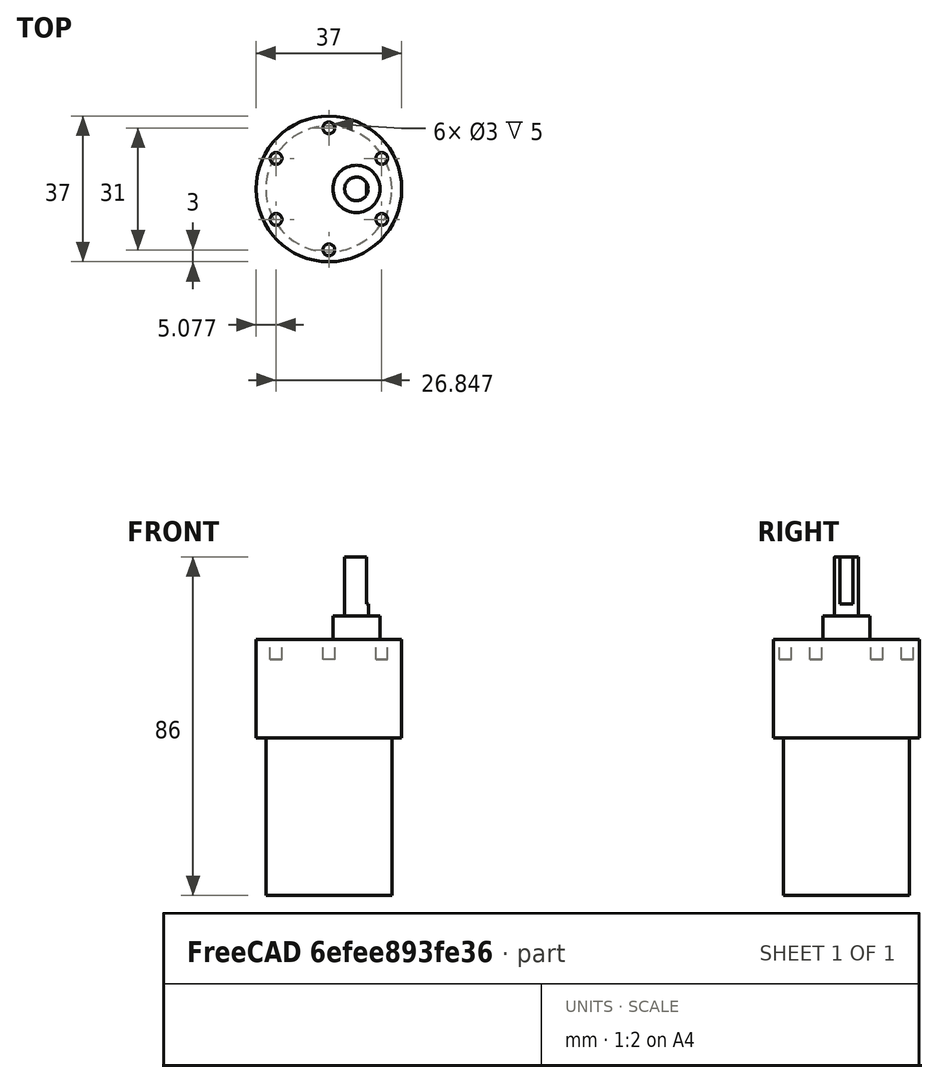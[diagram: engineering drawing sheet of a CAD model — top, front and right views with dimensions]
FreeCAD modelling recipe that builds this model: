
FCSTD DOCUMENT  (FreeCAD 0.17R13522 (Git))
Label: DC_Gear_Motor_37mm
License: All rights reserved
LicenseURL: http://en.wikipedia.org/wiki/All_rights_reserved
objects: Part::Cylinder×5, Part::MultiFuse×2, Part::Box×1, Part::FeaturePython×1, Part::Cut×1
note: 10 computed .brp shape members not serialized (recipe doc carries the construction recipe); baked Part::Feature solids carry a one-line shape summary decoded from their .brp

FEATURE [Part::Cylinder] Cylinder  label="Motor"
  Angle = 360
  AttacherType = Attacher::AttachEngine3D
  Height = 40
  Radius = 16
FEATURE [Part::Cylinder] Cylinder001  label="Gear Box"
  Angle = 360
  AttacherType = Attacher::AttachEngine3D
  Height = 25
  Placement = pos=(0,0,40) rot=(0,0,1;0rad)
  Radius = 18.5
FEATURE [Part::Cylinder] Cylinder002  label="Shaft Flange"
  Angle = 360
  AttacherType = Attacher::AttachEngine3D
  Height = 6
  Placement = pos=(7,0,65) rot=(0,0,1;0rad)
  Radius = 6
FEATURE [Part::Cylinder] Cylinder003  label="Shaft"
  Angle = 360
  AttacherType = Attacher::AttachEngine3D
  Height = 15
  Placement = pos=(7,0,71) rot=(0,0,1;0rad)
  Radius = 3
FEATURE [Part::Box] Box  label="Shaft D Cut Out"
  AttacherType = Attacher::AttachEngine3D
  Height = 12
  Length = 10
  Placement = pos=(9.5,-5,74) rot=(0,0,1;0rad)
  Width = 10
FEATURE [Part::Cylinder] Cylinder004  label="Screw"
  Angle = 360
  AttacherType = Attacher::AttachEngine3D
  Height = 5
  Placement = pos=(0,-15.5,60) rot=(0,0,1;0rad)
  Radius = 1.5
FEATURE [Part::FeaturePython] Array  label="Screw Array"  # Draft array (typed FeaturePython)
  Angle = 360
  ArrayType = 1
  Axis = (0,0,1)
  Base = -> Cylinder004
  Center = (0,0,0)
  Fuse = false
  IntervalAxis = (0,0,0)
  IntervalX = (1,0,0)
  IntervalY = (0,1,0)
  IntervalZ = (0,0,0)
  NumberPolar = 6
  NumberX = 1
  NumberY = 1
  NumberZ = 1
FEATURE [Part::MultiFuse] Fusion  label="Negative Fusion"
  Shapes = -> [Array,Box]
FEATURE [Part::MultiFuse] Fusion001  label="Positive Fusion"
  Shapes = -> [Cylinder,Cylinder001,Cylinder002,Cylinder003]
FEATURE [Part::Cut] Cut  label="DC Gear Motor 37mm"
  Base = -> Fusion001
  Tool = -> Fusion
